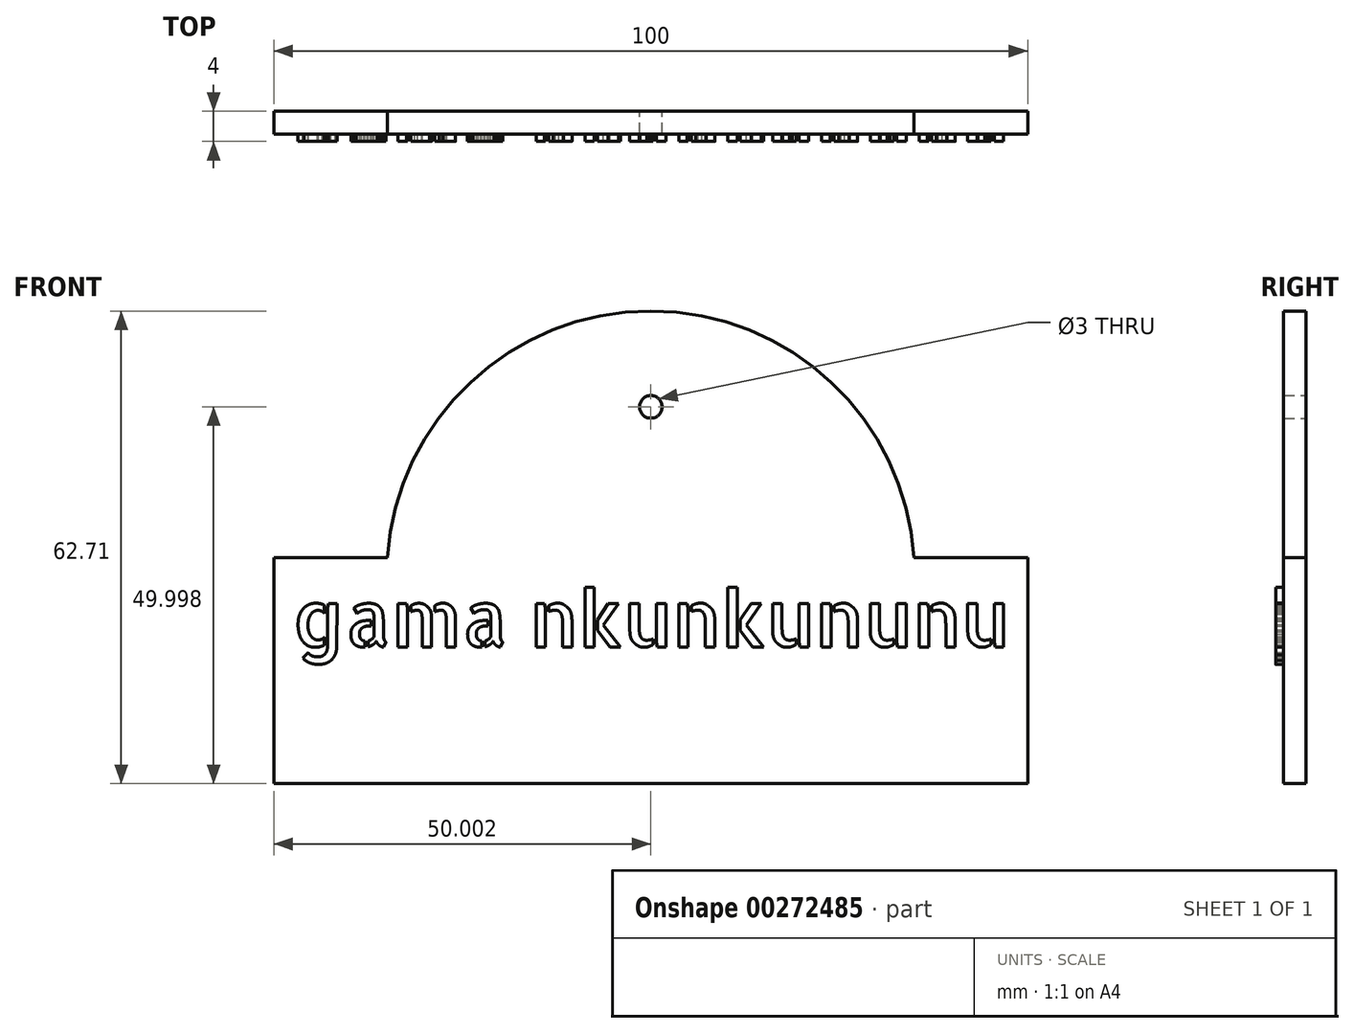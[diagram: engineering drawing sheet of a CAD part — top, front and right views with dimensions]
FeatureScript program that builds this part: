
annotation { "Feature Type Name" : "Feature", "Feature Type Description" : "" }
export const myFeature = defineFeature(function(context is Context, id is Id, definition is map)
    precondition{}
    {
        {
            var Q0;
            Q0=qCreatedBy(makeId("Front.planeOp"),FACE);
            var sketch = newSketch(context, id + "F0", { "sketchPlane" : qUnion([Q0])});
            skLineSegment(sketch, "E0.bottom", {"start": v(-49.95, 35.26) * mm, "end": v(50.05, 35.26) * mm});
            skLineSegment(sketch, "E0.top", {"start": v(-49.95, 5.26) * mm, "end": v(50.05, 5.26) * mm});
            skLineSegment(sketch, "E0.left", {"start": v(-49.95, 35.26) * mm, "end": v(-49.95, 5.26) * mm});
            skLineSegment(sketch, "E0.right", {"start": v(50.05, 35.26) * mm, "end": v(50.05, 5.26) * mm});
            skArc(sketch, "E1", {"start": v(34.98, 35.26) * mm, "mid": v(0.05, 67.97) * mm, "end": v(-34.87, 35.26) * mm});
            skCircle(sketch, "E2", {"center": v(0.05, 55.26) * mm, "radius": 1.5 * mm});
            skPoint(sketch, "E3", {"position": v(0.05, 35.26) * mm});
            skText(sketch, "E4", { "text": "gama nkunkununu", "fontName": "AllertaStencil-Regular.ttf"});
            const initialGuessF0  = {"E4": [-0.04745, 0.0234, 1, 0, 0.00753]};
            skSetInitialGuess(sketch, initialGuessF0);
            skSolve(sketch);
        }
        {
            var Q0;
            {var subQ0=sQuery(id+"F0.wireOp",EDGE,"E1");Q0=makeQuery(id+"F0.imprint","IMPRINT",FACE,{"disambiguationData":[TD([[makeQuery(id+"F0.imprint","IMPRINT",EDGE,{"derivedFrom":subQ0}),1.0]])]});}
            var Q1;
            Q1=makeQuery(id+"F0.imprint","IMPRINT",FACE,{"disambiguationData":[TD([[makeQuery(id+"F0.imprint","IMPRINT",EDGE,{"derivedFrom":sQuery(id+"F0.wireOp",EDGE,"E0.top")}),1.0]])]});
            extrude(context, id + "F1", {"entities" : qUnion([Q0, Q1]), "depth" : 3 * mm});
        }
        {
            var Q0;
            Q0=makeQuery(id+"F0.imprint","IMPRINT",FACE,{"disambiguationData":[TD([[makeQuery(id+"F0.imprint","IMPRINT",EDGE,{"derivedFrom":sQuery(id+"F0.wireOp",EDGE,"E4.sketch_text.stroke-0")}),-1.0]])]});
            var Q1;
            Q1=makeQuery(id+"F0.imprint","IMPRINT",FACE,{"disambiguationData":[TD([[makeQuery(id+"F0.imprint","IMPRINT",EDGE,{"derivedFrom":sQuery(id+"F0.wireOp",EDGE,"E4.sketch_text.stroke-26")}),-1.0]])]});
            var Q2;
            Q2=makeQuery(id+"F0.imprint","IMPRINT",FACE,{"disambiguationData":[TD([[makeQuery(id+"F0.imprint","IMPRINT",EDGE,{"derivedFrom":sQuery(id+"F0.wireOp",EDGE,"E4.sketch_text.stroke-43")}),-1.0]])]});
            var Q3;
            Q3=makeQuery(id+"F0.imprint","IMPRINT",FACE,{"disambiguationData":[TD([[makeQuery(id+"F0.imprint","IMPRINT",EDGE,{"derivedFrom":sQuery(id+"F0.wireOp",EDGE,"E4.sketch_text.stroke-62")}),-1.0]])]});
            var Q4;
            Q4=makeQuery(id+"F0.imprint","IMPRINT",FACE,{"disambiguationData":[TD([[makeQuery(id+"F0.imprint","IMPRINT",EDGE,{"derivedFrom":sQuery(id+"F0.wireOp",EDGE,"E4.sketch_text.stroke-98")}),-1.0]])]});
            var Q5;
            Q5=makeQuery(id+"F0.imprint","IMPRINT",FACE,{"disambiguationData":[TD([[makeQuery(id+"F0.imprint","IMPRINT",EDGE,{"derivedFrom":sQuery(id+"F0.wireOp",EDGE,"E4.sketch_text.stroke-119")}),-1.0]])]});
            var Q6;
            Q6=makeQuery(id+"F0.imprint","IMPRINT",FACE,{"disambiguationData":[TD([[makeQuery(id+"F0.imprint","IMPRINT",EDGE,{"derivedFrom":sQuery(id+"F0.wireOp",EDGE,"E4.sketch_text.stroke-103")}),-1.0]])]});
            var Q7;
            Q7=makeQuery(id+"F0.imprint","IMPRINT",FACE,{"disambiguationData":[TD([[makeQuery(id+"F0.imprint","IMPRINT",EDGE,{"derivedFrom":sQuery(id+"F0.wireOp",EDGE,"E4.sketch_text.stroke-137")}),-1.0]])]});
            var Q8;
            Q8=makeQuery(id+"F0.imprint","IMPRINT",FACE,{"disambiguationData":[TD([[makeQuery(id+"F0.imprint","IMPRINT",EDGE,{"derivedFrom":sQuery(id+"F0.wireOp",EDGE,"E4.sketch_text.stroke-156")}),-1.0]])]});
            var Q9;
            Q9=makeQuery(id+"F0.imprint","IMPRINT",FACE,{"disambiguationData":[TD([[makeQuery(id+"F0.imprint","IMPRINT",EDGE,{"derivedFrom":sQuery(id+"F0.wireOp",EDGE,"E4.sketch_text.stroke-192")}),-1.0]])]});
            extrude(context, id + "F2", {"entities" : qUnion([Q0, Q1, Q2, Q3, Q4, Q5, Q6, Q7, Q8, Q9]), "operationType" : NewBodyOperationType.ADD, "depth" : 4 * mm});
        }
        {
            var Q0;
            Q0=makeQuery(id+"F0.imprint","IMPRINT",FACE,{"disambiguationData":[TD([[makeQuery(id+"F0.imprint","IMPRINT",EDGE,{"derivedFrom":sQuery(id+"F0.wireOp",EDGE,"E4.sketch_text.stroke-405")}),-1.0]])]});
            var Q1;
            Q1=makeQuery(id+"F0.imprint","IMPRINT",FACE,{"disambiguationData":[TD([[makeQuery(id+"F0.imprint","IMPRINT",EDGE,{"derivedFrom":sQuery(id+"F0.wireOp",EDGE,"E4.sketch_text.stroke-385")}),-1.0]])]});
            var Q2;
            Q2=makeQuery(id+"F0.imprint","IMPRINT",FACE,{"disambiguationData":[TD([[makeQuery(id+"F0.imprint","IMPRINT",EDGE,{"derivedFrom":sQuery(id+"F0.wireOp",EDGE,"E4.sketch_text.stroke-366")}),-1.0]])]});
            var Q3;
            Q3=makeQuery(id+"F0.imprint","IMPRINT",FACE,{"disambiguationData":[TD([[makeQuery(id+"F0.imprint","IMPRINT",EDGE,{"derivedFrom":sQuery(id+"F0.wireOp",EDGE,"E4.sketch_text.stroke-361")}),-1.0]])]});
            var Q4;
            Q4=makeQuery(id+"F0.imprint","IMPRINT",FACE,{"disambiguationData":[TD([[makeQuery(id+"F0.imprint","IMPRINT",EDGE,{"derivedFrom":sQuery(id+"F0.wireOp",EDGE,"E4.sketch_text.stroke-356")}),-1.0]])]});
            var Q5;
            Q5=makeQuery(id+"F0.imprint","IMPRINT",FACE,{"disambiguationData":[TD([[makeQuery(id+"F0.imprint","IMPRINT",EDGE,{"derivedFrom":sQuery(id+"F0.wireOp",EDGE,"E4.sketch_text.stroke-336")}),-1.0]])]});
            var Q6;
            Q6=makeQuery(id+"F0.imprint","IMPRINT",FACE,{"disambiguationData":[TD([[makeQuery(id+"F0.imprint","IMPRINT",EDGE,{"derivedFrom":sQuery(id+"F0.wireOp",EDGE,"E4.sketch_text.stroke-317")}),-1.0]])]});
            var Q7;
            Q7=makeQuery(id+"F0.imprint","IMPRINT",FACE,{"disambiguationData":[TD([[makeQuery(id+"F0.imprint","IMPRINT",EDGE,{"derivedFrom":sQuery(id+"F0.wireOp",EDGE,"E4.sketch_text.stroke-312")}),-1.0]])]});
            var Q8;
            Q8=makeQuery(id+"F0.imprint","IMPRINT",FACE,{"disambiguationData":[TD([[makeQuery(id+"F0.imprint","IMPRINT",EDGE,{"derivedFrom":sQuery(id+"F0.wireOp",EDGE,"E4.sketch_text.stroke-307")}),-1.0]])]});
            var Q9;
            Q9=makeQuery(id+"F0.imprint","IMPRINT",FACE,{"disambiguationData":[TD([[makeQuery(id+"F0.imprint","IMPRINT",EDGE,{"derivedFrom":sQuery(id+"F0.wireOp",EDGE,"E4.sketch_text.stroke-287")}),-1.0]])]});
            var Q10;
            Q10=makeQuery(id+"F0.imprint","IMPRINT",FACE,{"disambiguationData":[TD([[makeQuery(id+"F0.imprint","IMPRINT",EDGE,{"derivedFrom":sQuery(id+"F0.wireOp",EDGE,"E4.sketch_text.stroke-276")}),-1.0]])]});
            var Q11;
            Q11=makeQuery(id+"F0.imprint","IMPRINT",FACE,{"disambiguationData":[TD([[makeQuery(id+"F0.imprint","IMPRINT",EDGE,{"derivedFrom":sQuery(id+"F0.wireOp",EDGE,"E4.sketch_text.stroke-283")}),-1.0]])]});
            var Q12;
            Q12=makeQuery(id+"F0.imprint","IMPRINT",FACE,{"disambiguationData":[TD([[makeQuery(id+"F0.imprint","IMPRINT",EDGE,{"derivedFrom":sQuery(id+"F0.wireOp",EDGE,"E4.sketch_text.stroke-257")}),-1.0]])]});
            var Q13;
            Q13=makeQuery(id+"F0.imprint","IMPRINT",FACE,{"disambiguationData":[TD([[makeQuery(id+"F0.imprint","IMPRINT",EDGE,{"derivedFrom":sQuery(id+"F0.wireOp",EDGE,"E4.sketch_text.stroke-252")}),-1.0]])]});
            var Q14;
            Q14=makeQuery(id+"F0.imprint","IMPRINT",FACE,{"disambiguationData":[TD([[makeQuery(id+"F0.imprint","IMPRINT",EDGE,{"derivedFrom":sQuery(id+"F0.wireOp",EDGE,"E4.sketch_text.stroke-247")}),-1.0]])]});
            var Q15;
            Q15=makeQuery(id+"F0.imprint","IMPRINT",FACE,{"disambiguationData":[TD([[makeQuery(id+"F0.imprint","IMPRINT",EDGE,{"derivedFrom":sQuery(id+"F0.wireOp",EDGE,"E4.sketch_text.stroke-227")}),-1.0]])]});
            var Q16;
            Q16=makeQuery(id+"F0.imprint","IMPRINT",FACE,{"disambiguationData":[TD([[makeQuery(id+"F0.imprint","IMPRINT",EDGE,{"derivedFrom":sQuery(id+"F0.wireOp",EDGE,"E4.sketch_text.stroke-216")}),-1.0]])]});
            var Q17;
            Q17=makeQuery(id+"F0.imprint","IMPRINT",FACE,{"disambiguationData":[TD([[makeQuery(id+"F0.imprint","IMPRINT",EDGE,{"derivedFrom":sQuery(id+"F0.wireOp",EDGE,"E4.sketch_text.stroke-223")}),-1.0]])]});
            var Q18;
            Q18=makeQuery(id+"F0.imprint","IMPRINT",FACE,{"disambiguationData":[TD([[makeQuery(id+"F0.imprint","IMPRINT",EDGE,{"derivedFrom":sQuery(id+"F0.wireOp",EDGE,"E4.sketch_text.stroke-197")}),-1.0]])]});
            var Q19;
            Q19=makeQuery(id+"F0.imprint","IMPRINT",FACE,{"disambiguationData":[TD([[makeQuery(id+"F0.imprint","IMPRINT",EDGE,{"derivedFrom":sQuery(id+"F0.wireOp",EDGE,"E4.sketch_text.stroke-192")}),-1.0]])]});
            var Q20;
            Q20=makeQuery(id+"F0.imprint","IMPRINT",FACE,{"disambiguationData":[TD([[makeQuery(id+"F0.imprint","IMPRINT",EDGE,{"derivedFrom":sQuery(id+"F0.wireOp",EDGE,"E4.sketch_text.stroke-156")}),-1.0]])]});
            var Q21;
            Q21=makeQuery(id+"F0.imprint","IMPRINT",FACE,{"disambiguationData":[TD([[makeQuery(id+"F0.imprint","IMPRINT",EDGE,{"derivedFrom":sQuery(id+"F0.wireOp",EDGE,"E4.sketch_text.stroke-137")}),-1.0]])]});
            var Q22;
            Q22=makeQuery(id+"F0.imprint","IMPRINT",FACE,{"disambiguationData":[TD([[makeQuery(id+"F0.imprint","IMPRINT",EDGE,{"derivedFrom":sQuery(id+"F0.wireOp",EDGE,"E4.sketch_text.stroke-103")}),-1.0]])]});
            var Q23;
            Q23=makeQuery(id+"F0.imprint","IMPRINT",FACE,{"disambiguationData":[TD([[makeQuery(id+"F0.imprint","IMPRINT",EDGE,{"derivedFrom":sQuery(id+"F0.wireOp",EDGE,"E4.sketch_text.stroke-119")}),-1.0]])]});
            var Q24;
            Q24=makeQuery(id+"F0.imprint","IMPRINT",FACE,{"disambiguationData":[TD([[makeQuery(id+"F0.imprint","IMPRINT",EDGE,{"derivedFrom":sQuery(id+"F0.wireOp",EDGE,"E4.sketch_text.stroke-98")}),-1.0]])]});
            var Q25;
            Q25=makeQuery(id+"F0.imprint","IMPRINT",FACE,{"disambiguationData":[TD([[makeQuery(id+"F0.imprint","IMPRINT",EDGE,{"derivedFrom":sQuery(id+"F0.wireOp",EDGE,"E4.sketch_text.stroke-62")}),-1.0]])]});
            var Q26;
            Q26=makeQuery(id+"F0.imprint","IMPRINT",FACE,{"disambiguationData":[TD([[makeQuery(id+"F0.imprint","IMPRINT",EDGE,{"derivedFrom":sQuery(id+"F0.wireOp",EDGE,"E4.sketch_text.stroke-43")}),-1.0]])]});
            var Q27;
            Q27=makeQuery(id+"F0.imprint","IMPRINT",FACE,{"disambiguationData":[TD([[makeQuery(id+"F0.imprint","IMPRINT",EDGE,{"derivedFrom":sQuery(id+"F0.wireOp",EDGE,"E4.sketch_text.stroke-26")}),-1.0]])]});
            var Q28;
            Q28=makeQuery(id+"F0.imprint","IMPRINT",FACE,{"disambiguationData":[TD([[makeQuery(id+"F0.imprint","IMPRINT",EDGE,{"derivedFrom":sQuery(id+"F0.wireOp",EDGE,"E4.sketch_text.stroke-0")}),-1.0]])]});
            extrude(context, id + "F3", {"entities" : qUnion([Q0, Q1, Q2, Q3, Q4, Q5, Q6, Q7, Q8, Q9, Q10, Q11, Q12, Q13, Q14, Q15, Q16, Q17, Q18, Q19, Q20, Q21, Q22, Q23, Q24, Q25, Q26, Q27, Q28]), "operationType" : NewBodyOperationType.ADD, "depth" : 4 * mm});
        }
    });
